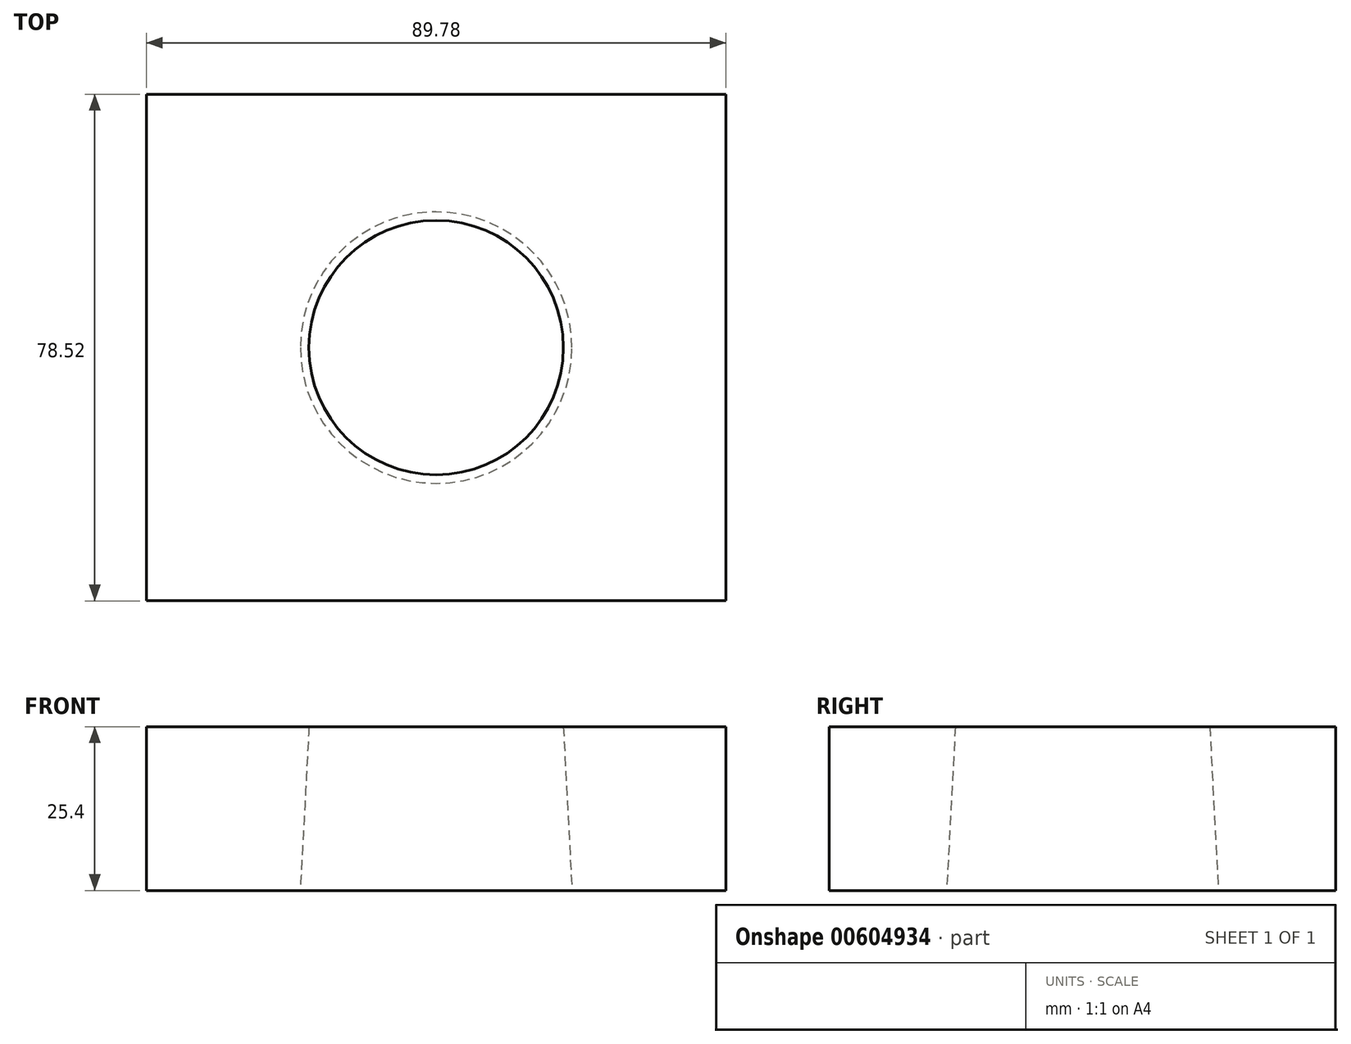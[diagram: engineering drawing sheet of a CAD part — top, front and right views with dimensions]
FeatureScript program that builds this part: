
annotation { "Feature Type Name" : "Feature", "Feature Type Description" : "" }
export const myFeature = defineFeature(function(context is Context, id is Id, definition is map)
    precondition{}
    {
        {
            var Q0;
            Q0=qCreatedBy(makeId("Top.planeOp"),FACE);
            var sketch = newSketch(context, id + "F0", { "sketchPlane" : qUnion([Q0])});
            skLineSegment(sketch, "E0.bottom", {"start": v(44.9, 39.26) * mm, "end": v(-44.9, 39.26) * mm});
            skLineSegment(sketch, "E0.top", {"start": v(44.9, -39.26) * mm, "end": v(-44.9, -39.26) * mm});
            skLineSegment(sketch, "E0.left", {"start": v(44.9, 39.26) * mm, "end": v(44.9, -39.26) * mm});
            skLineSegment(sketch, "E0.right", {"start": v(-44.9, 39.26) * mm, "end": v(-44.9, -39.26) * mm});
            skPoint(sketch, "E0.middle", {"position": v(0, 0) * mm});
            skSolve(sketch);
        }
        {
            var Q0;
            Q0=makeQuery(id+"F0.imprint","IMPRINT",FACE,{"disambiguationData":[TD([[makeQuery(id+"F0.imprint","IMPRINT",EDGE,{"derivedFrom":sQuery(id+"F0.wireOp",EDGE,"E0.bottom")}),1.0]])]});
            extrude(context, id + "F1", {"entities" : qUnion([Q0]), "endBound" : BoundingType.SYMMETRIC, "oppositeDirection" : true, "depth" : 25.4 * mm, "offsetDistance" : 25.4 * mm});
        }
        {
            var Q0;
            Q0=makeQuery(id+"F1.opExtrude","CAP_FACE",FACE,{"disambiguationData":[OSD([sQuery(id+"F0.wireOp",EDGE,"E0.bottom"),sQuery(id+"F0.wireOp",EDGE,"E0.top"),sQuery(id+"F0.wireOp",EDGE,"E0.left"),sQuery(id+"F0.wireOp",EDGE,"E0.right")])],"isStart":true});
            var sketch = newSketch(context, id + "F2", { "sketchPlane" : qUnion([Q0])});
            skCircle(sketch, "E1", {"center": v(0, 0) * mm, "radius": 19.71 * mm});
            skSolve(sketch);
        }
        {
            var Q0;
            Q0=makeQuery(id+"F2.imprint","IMPRINT",FACE,{"disambiguationData":[TD([[makeQuery(id+"F2.imprint","IMPRINT",EDGE,{"derivedFrom":sQuery(id+"F2.wireOp",EDGE,"E1")}),1.0]])]});
            extrude(context, id + "F3", {"entities" : qUnion([Q0]), "operationType" : NewBodyOperationType.REMOVE, "oppositeDirection" : true, "depth" : 25.4 * mm, "offsetDistance" : 25.4 * mm, "hasDraft" : true, "draftAngle" : 3 * degree, "hasSecondDirection" : true, "secondDirectionOppositeDirection" : false, "secondDirectionDepth" : 25.4 * mm});
        }
    });
